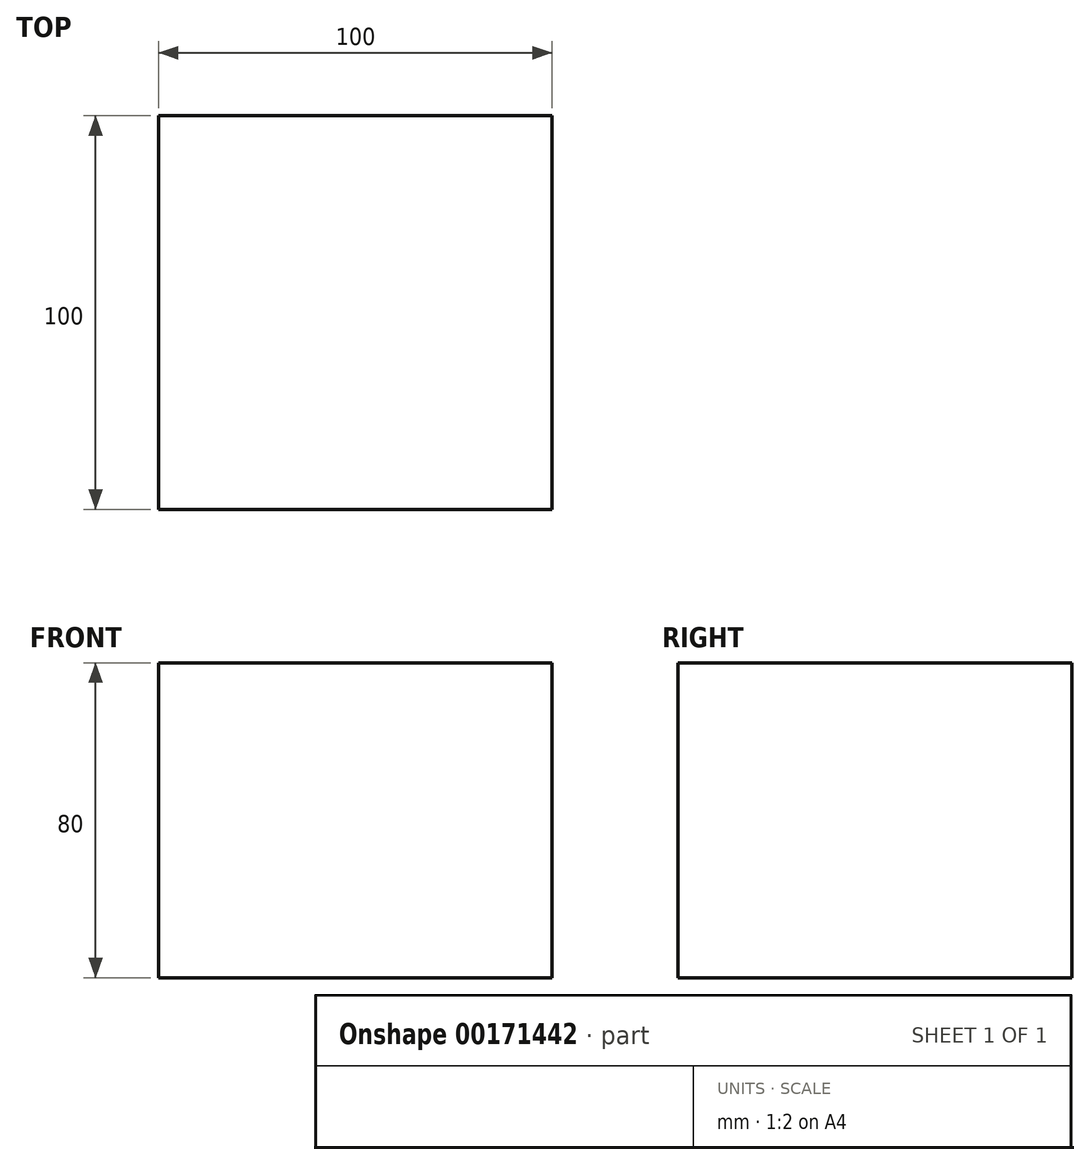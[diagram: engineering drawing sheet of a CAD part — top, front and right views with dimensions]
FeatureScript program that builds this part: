
annotation { "Feature Type Name" : "Feature", "Feature Type Description" : "" }
export const myFeature = defineFeature(function(context is Context, id is Id, definition is map)
    precondition{}
    {
        {
            var Q0;
            Q0=qCreatedBy(makeId("Top.planeOp"),FACE);
            var sketch = newSketch(context, id + "F0", { "sketchPlane" : qUnion([Q0])});
            skLineSegment(sketch, "E0.bottom", {"start": v(50, 20) * mm, "end": v(-50, 20) * mm});
            skLineSegment(sketch, "E0.top", {"start": v(50, -20) * mm, "end": v(-50, -20) * mm});
            skLineSegment(sketch, "E0.left", {"start": v(50, 20) * mm, "end": v(50, -20) * mm});
            skLineSegment(sketch, "E0.right", {"start": v(-50, 20) * mm, "end": v(-50, -20) * mm});
            skPoint(sketch, "E0.middle", {"position": v(0, 0) * mm});
            skSolve(sketch);
        }
        {
            var Q0;
            Q0 = qSketchRegion(id + "F0", true);
            extrude(context, id + "F1", {"entities" : qUnion([Q0]), "depth" : 80 * mm});
        }
        {
            var Q0;
            Q0=makeQuery(id+"F1.opExtrude","SWEPT_FACE",FACE,{"disambiguationData":[OSD([sQuery(id+"F0.wireOp",EDGE,"E0.bottom")])]});
            extrude(context, id + "F2", {"entities" : qUnion([Q0]), "operationType" : NewBodyOperationType.ADD, "depth" : 60 * mm});
        }
    });
